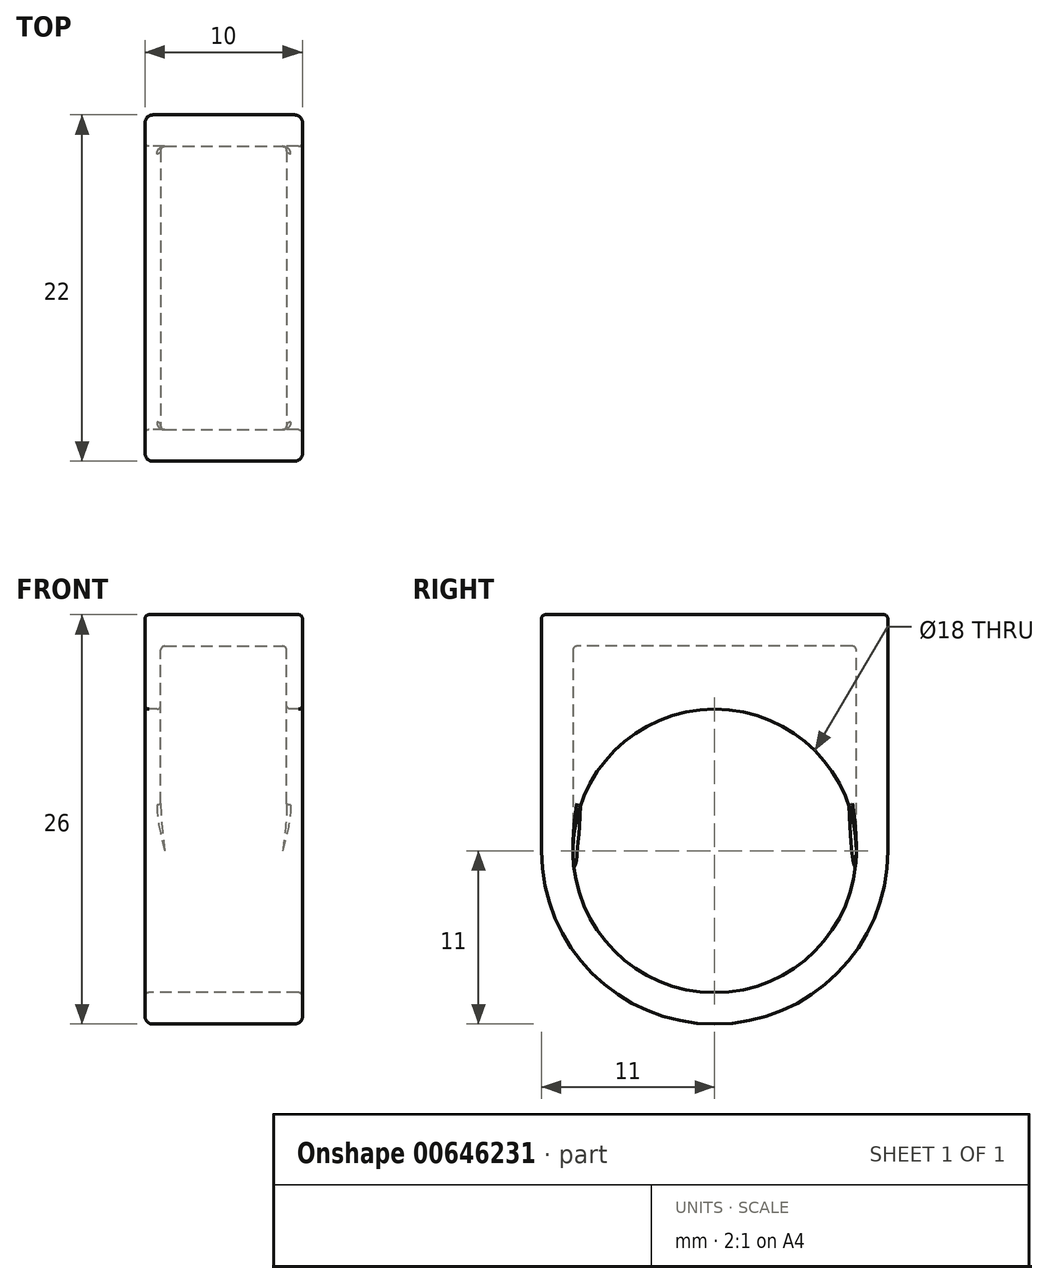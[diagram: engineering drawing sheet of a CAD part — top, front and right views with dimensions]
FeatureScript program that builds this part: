
annotation { "Feature Type Name" : "Feature", "Feature Type Description" : "" }
export const myFeature = defineFeature(function(context is Context, id is Id, definition is map)
    precondition{}
    {
        {
            var Q0;
            Q0=qCreatedBy(makeId("Right.planeOp"),FACE);
            var sketch = newSketch(context, id + "F0", { "sketchPlane" : qUnion([Q0])});
            skCircle(sketch, "E0", {"center": v(0, 0) * mm, "radius": 9 * mm});
            skArc(sketch, "E1", {"start": v(-11, 0) * mm, "mid": v(0, -11) * mm, "end": v(11, 0) * mm});
            skLineSegment(sketch, "E2", {"start": v(-11, 0) * mm, "end": v(-11, 15) * mm});
            skLineSegment(sketch, "E3", {"start": v(11, 0) * mm, "end": v(11, 15) * mm});
            skLineSegment(sketch, "E4", {"start": v(-11, 15) * mm, "end": v(11, 15) * mm});
            skSolve(sketch);
        }
        {
            var Q0;
            Q0 = qSketchRegion(id + "F0", true);
            extrude(context, id + "F1", {"entities" : qUnion([Q0]), "endBound" : BoundingType.SYMMETRIC, "depth" : 10 * mm, "offsetDistance" : 25 * mm});
        }
        {
            var Q0;
            Q0=qCreatedBy(makeId("Right.planeOp"),FACE);
            var sketch = newSketch(context, id + "F2", { "sketchPlane" : qUnion([Q0])});
            skLineSegment(sketch, "E5.0", {"start": v(9, 13) * mm, "end": v(-9, 13) * mm});
            skLineSegment(sketch, "E5.1", {"start": v(9, 0) * mm, "end": v(9, 13) * mm});
            skArc(sketch, "E5.2", {"start": v(-9, 0) * mm, "mid": v(0, -9) * mm, "end": v(9, 0) * mm});
            skLineSegment(sketch, "E5.3", {"start": v(-9, 13) * mm, "end": v(-9, 0) * mm});
            skSolve(sketch);
        }
        {
            var Q0;
            Q0 = qSketchRegion(id + "F2", true);
            extrude(context, id + "F3", {"entities" : qUnion([Q0]), "operationType" : NewBodyOperationType.REMOVE, "endBound" : BoundingType.SYMMETRIC, "oppositeDirection" : true, "depth" : 8 * mm, "offsetDistance" : 25 * mm});
        }
        {
            var Q0;
            Q0=makeQuery(id+"F1.opExtrude","CAP_EDGE",EDGE,{"disambiguationData":[OSD([sQuery(id+"F0.wireOp",EDGE,"E2")])],"isStart":false});
            var Q1;
            Q1=makeQuery(id+"F1.opExtrude","CAP_EDGE",EDGE,{"disambiguationData":[OSD([sQuery(id+"F0.wireOp",EDGE,"E2")])],"isStart":true});
            fillet(context, id + "F4", {"entities" : qUnion([Q0, Q1]), "radius" : .5 * mm, "tangentPropagation" : true, "allowEdgeOverflow" : false});
        }
        {
            var Q0;
            {var subQ0=sQuery(id+"F0.wireOp",EDGE,"E1");Q0=makeQuery(id+"F4.opFillet","BLEND_EDGE",EDGE,{"blendedFrom":[makeQuery(id+"F1.opExtrude","CAP_EDGE",EDGE,{"disambiguationData":[OSD([subQ0])],"isStart":true}),makeQuery(id+"F1.opExtrude","CAP_FACE",FACE,{"disambiguationData":[OSD([sQuery(id+"F0.wireOp",EDGE,"E0"),subQ0,sQuery(id+"F0.wireOp",EDGE,"E2"),sQuery(id+"F0.wireOp",EDGE,"E3"),sQuery(id+"F0.wireOp",EDGE,"E4")])],"isStart":true})],"blendedInto":[makeQuery(id+"F1.opExtrude","CAP_FACE",FACE,{"disambiguationData":[OSD([sQuery(id+"F0.wireOp",EDGE,"E0"),subQ0,sQuery(id+"F0.wireOp",EDGE,"E2"),sQuery(id+"F0.wireOp",EDGE,"E3"),sQuery(id+"F0.wireOp",EDGE,"E4")])],"isStart":true})]});}
            var Q1;
            Q1=makeQuery(id+"F1.opExtrude","CAP_EDGE",EDGE,{"disambiguationData":[OSD([sQuery(id+"F0.wireOp",EDGE,"E0")])],"isStart":true});
            var Q2;
            Q2=makeQuery(id+"F4.opFillet","BLEND_EDGE",EDGE,{"blendedFrom":[makeQuery(id+"F1.opExtrude","CAP_EDGE",EDGE,{"disambiguationData":[OSD([sQuery(id+"F0.wireOp",EDGE,"E2")])],"isStart":true}),makeQuery(id+"F1.opExtrude","SWEPT_FACE",FACE,{"disambiguationData":[OSD([sQuery(id+"F0.wireOp",EDGE,"E4")])]})],"blendedInto":[makeQuery(id+"F1.opExtrude","SWEPT_FACE",FACE,{"disambiguationData":[OSD([sQuery(id+"F0.wireOp",EDGE,"E4")])]})]});
            var Q3;
            Q3=makeQuery(id+"F3.boolean.opBoolean","COPY",EDGE,{"derivedFrom":makeQuery(id+"F3.opExtrude","SWEPT_EDGE",EDGE,{"disambiguationData":[OSD([sQuery(id+"F2.wireOp",EDGE,"E5.1"),sQuery(id+"F2.wireOp",EDGE,"E5.2")])]})});
            var Q4;
            Q4=makeQuery(id+"F3.boolean.opBoolean","INTERSECT",EDGE,{"derivedFrom":[makeQuery(id+"F1.opExtrude","SWEPT_FACE",FACE,{"disambiguationData":[OSD([sQuery(id+"F0.wireOp",EDGE,"E0")])]}),makeQuery(id+"F3.opExtrude","CAP_FACE",FACE,{"disambiguationData":[OSD([sQuery(id+"F2.wireOp",EDGE,"E5.0"),sQuery(id+"F2.wireOp",EDGE,"E5.1"),sQuery(id+"F2.wireOp",EDGE,"E5.2"),sQuery(id+"F2.wireOp",EDGE,"E5.3")])],"isStart":false})]});
            var Q5;
            {var subQ0=sQuery(id+"F0.wireOp",EDGE,"E1");Q5=makeQuery(id+"F4.opFillet","BLEND_EDGE",EDGE,{"blendedFrom":[makeQuery(id+"F1.opExtrude","CAP_EDGE",EDGE,{"disambiguationData":[OSD([subQ0])],"isStart":true}),makeQuery(id+"F1.opExtrude","SWEPT_FACE",FACE,{"disambiguationData":[OSD([subQ0])]})],"blendedInto":[makeQuery(id+"F1.opExtrude","SWEPT_FACE",FACE,{"disambiguationData":[OSD([subQ0])]})]});}
            var Q6;
            {var subQ0=sQuery(id+"F0.wireOp",EDGE,"E1");Q6=makeQuery(id+"F4.opFillet","BLEND_EDGE",EDGE,{"blendedFrom":[makeQuery(id+"F1.opExtrude","CAP_EDGE",EDGE,{"disambiguationData":[OSD([subQ0])],"isStart":false}),makeQuery(id+"F1.opExtrude","SWEPT_FACE",FACE,{"disambiguationData":[OSD([subQ0])]})],"blendedInto":[makeQuery(id+"F1.opExtrude","SWEPT_FACE",FACE,{"disambiguationData":[OSD([subQ0])]})]});}
            var Q7;
            Q7=makeQuery(id+"F1.opExtrude","CAP_EDGE",EDGE,{"disambiguationData":[OSD([sQuery(id+"F0.wireOp",EDGE,"E4")])],"isStart":true});
            var Q8;
            Q8=makeQuery(id+"F1.opExtrude","CAP_EDGE",EDGE,{"disambiguationData":[OSD([sQuery(id+"F0.wireOp",EDGE,"E4")])],"isStart":false});
            var Q9;
            Q9=makeQuery(id+"F4.opFillet","BLEND_EDGE",EDGE,{"blendedFrom":[makeQuery(id+"F1.opExtrude","CAP_EDGE",EDGE,{"disambiguationData":[OSD([sQuery(id+"F0.wireOp",EDGE,"E1")])],"isStart":true}),makeQuery(id+"F1.opExtrude","CAP_EDGE",EDGE,{"disambiguationData":[OSD([sQuery(id+"F0.wireOp",EDGE,"E2")])],"isStart":true})],"blendedInto":[]});
            var Q10;
            Q10=makeQuery(id+"F1.opExtrude","SWEPT_EDGE",EDGE,{"disambiguationData":[OSD([sQuery(id+"F0.wireOp",EDGE,"E3"),sQuery(id+"F0.wireOp",EDGE,"E4")])]});
            var Q11;
            Q11=makeQuery(id+"F4.opFillet","BLEND_EDGE",EDGE,{"blendedFrom":[makeQuery(id+"F1.opExtrude","CAP_EDGE",EDGE,{"disambiguationData":[OSD([sQuery(id+"F0.wireOp",EDGE,"E1")])],"isStart":true}),makeQuery(id+"F1.opExtrude","CAP_EDGE",EDGE,{"disambiguationData":[OSD([sQuery(id+"F0.wireOp",EDGE,"E3")])],"isStart":true})],"blendedInto":[]});
            var Q12;
            Q12=makeQuery(id+"F1.opExtrude","SWEPT_EDGE",EDGE,{"disambiguationData":[OSD([sQuery(id+"F0.wireOp",EDGE,"E2"),sQuery(id+"F0.wireOp",EDGE,"E4")])]});
            var Q13;
            Q13=makeQuery(id+"F1.opExtrude","CAP_EDGE",EDGE,{"disambiguationData":[OSD([sQuery(id+"F0.wireOp",EDGE,"E0")])],"isStart":false});
            var Q14;
            Q14=makeQuery(id+"F1.opExtrude","SWEPT_EDGE",EDGE,{"disambiguationData":[OSD([sQuery(id+"F0.wireOp",EDGE,"E1"),sQuery(id+"F0.wireOp",EDGE,"E3")])]});
            var Q15;
            Q15=makeQuery(id+"F1.opExtrude","SWEPT_EDGE",EDGE,{"disambiguationData":[OSD([sQuery(id+"F0.wireOp",EDGE,"E1"),sQuery(id+"F0.wireOp",EDGE,"E2")])]});
            var Q16;
            {var subQ0=sQuery(id+"F0.wireOp",EDGE,"E2");Q16=makeQuery(id+"F4.opFillet","BLEND_EDGE",EDGE,{"blendedFrom":[makeQuery(id+"F1.opExtrude","CAP_EDGE",EDGE,{"disambiguationData":[OSD([subQ0])],"isStart":false}),makeQuery(id+"F1.opExtrude","CAP_FACE",FACE,{"disambiguationData":[OSD([sQuery(id+"F0.wireOp",EDGE,"E0"),sQuery(id+"F0.wireOp",EDGE,"E1"),subQ0,sQuery(id+"F0.wireOp",EDGE,"E3"),sQuery(id+"F0.wireOp",EDGE,"E4")])],"isStart":false})],"blendedInto":[makeQuery(id+"F1.opExtrude","CAP_FACE",FACE,{"disambiguationData":[OSD([sQuery(id+"F0.wireOp",EDGE,"E0"),sQuery(id+"F0.wireOp",EDGE,"E1"),subQ0,sQuery(id+"F0.wireOp",EDGE,"E3"),sQuery(id+"F0.wireOp",EDGE,"E4")])],"isStart":false})]});}
            var Q17;
            {var subQ0=sQuery(id+"F0.wireOp",EDGE,"E2");Q17=makeQuery(id+"F4.opFillet","BLEND_EDGE",EDGE,{"blendedFrom":[makeQuery(id+"F1.opExtrude","CAP_EDGE",EDGE,{"disambiguationData":[OSD([subQ0])],"isStart":true}),makeQuery(id+"F1.opExtrude","SWEPT_FACE",FACE,{"disambiguationData":[OSD([subQ0])]})],"blendedInto":[makeQuery(id+"F1.opExtrude","SWEPT_FACE",FACE,{"disambiguationData":[OSD([subQ0])]})]});}
            var Q18;
            Q18=makeQuery(id+"F3.boolean.opBoolean","COPY",EDGE,{"derivedFrom":makeQuery(id+"F3.opExtrude","SWEPT_EDGE",EDGE,{"disambiguationData":[OSD([sQuery(id+"F2.wireOp",EDGE,"E5.0"),sQuery(id+"F2.wireOp",EDGE,"E5.1")])]})});
            var Q19;
            Q19=makeQuery(id+"F3.boolean.opBoolean","COPY",EDGE,{"derivedFrom":makeQuery(id+"F3.opExtrude","SWEPT_EDGE",EDGE,{"disambiguationData":[OSD([sQuery(id+"F2.wireOp",EDGE,"E5.0"),sQuery(id+"F2.wireOp",EDGE,"E5.3")])]})});
            var Q20;
            Q20=makeQuery(id+"F3.boolean.opBoolean","COPY",EDGE,{"derivedFrom":makeQuery(id+"F3.opExtrude","SWEPT_EDGE",EDGE,{"disambiguationData":[OSD([sQuery(id+"F2.wireOp",EDGE,"E5.2"),sQuery(id+"F2.wireOp",EDGE,"E5.3")])]})});
            var Q21;
            Q21=makeQuery(id+"F3.boolean.opBoolean","COPY",EDGE,{"derivedFrom":makeQuery(id+"F3.opExtrude","CAP_EDGE",EDGE,{"disambiguationData":[OSD([sQuery(id+"F2.wireOp",EDGE,"E5.0")])],"isStart":true})});
            var Q22;
            Q22=makeQuery(id+"F3.boolean.opBoolean","COPY",EDGE,{"derivedFrom":makeQuery(id+"F3.opExtrude","CAP_EDGE",EDGE,{"disambiguationData":[OSD([sQuery(id+"F2.wireOp",EDGE,"E5.0")])],"isStart":false})});
            var Q23;
            Q23=makeQuery(id+"F3.boolean.opBoolean","COPY",EDGE,{"derivedFrom":makeQuery(id+"F3.opExtrude","CAP_EDGE",EDGE,{"disambiguationData":[OSD([sQuery(id+"F2.wireOp",EDGE,"E5.1")])],"isStart":false})});
            var Q24;
            {var subQ0=sQuery(id+"F0.wireOp",EDGE,"E1");Q24=makeQuery(id+"F4.opFillet","BLEND_EDGE",EDGE,{"blendedFrom":[makeQuery(id+"F1.opExtrude","CAP_EDGE",EDGE,{"disambiguationData":[OSD([subQ0])],"isStart":false}),makeQuery(id+"F1.opExtrude","CAP_FACE",FACE,{"disambiguationData":[OSD([sQuery(id+"F0.wireOp",EDGE,"E0"),subQ0,sQuery(id+"F0.wireOp",EDGE,"E2"),sQuery(id+"F0.wireOp",EDGE,"E3"),sQuery(id+"F0.wireOp",EDGE,"E4")])],"isStart":false})],"blendedInto":[makeQuery(id+"F1.opExtrude","CAP_FACE",FACE,{"disambiguationData":[OSD([sQuery(id+"F0.wireOp",EDGE,"E0"),subQ0,sQuery(id+"F0.wireOp",EDGE,"E2"),sQuery(id+"F0.wireOp",EDGE,"E3"),sQuery(id+"F0.wireOp",EDGE,"E4")])],"isStart":false})]});}
            var Q25;
            {var subQ0=sQuery(id+"F0.wireOp",EDGE,"E2");Q25=makeQuery(id+"F4.opFillet","BLEND_EDGE",EDGE,{"blendedFrom":[makeQuery(id+"F1.opExtrude","CAP_EDGE",EDGE,{"disambiguationData":[OSD([subQ0])],"isStart":true}),makeQuery(id+"F1.opExtrude","CAP_FACE",FACE,{"disambiguationData":[OSD([sQuery(id+"F0.wireOp",EDGE,"E0"),sQuery(id+"F0.wireOp",EDGE,"E1"),subQ0,sQuery(id+"F0.wireOp",EDGE,"E3"),sQuery(id+"F0.wireOp",EDGE,"E4")])],"isStart":true})],"blendedInto":[makeQuery(id+"F1.opExtrude","CAP_FACE",FACE,{"disambiguationData":[OSD([sQuery(id+"F0.wireOp",EDGE,"E0"),sQuery(id+"F0.wireOp",EDGE,"E1"),subQ0,sQuery(id+"F0.wireOp",EDGE,"E3"),sQuery(id+"F0.wireOp",EDGE,"E4")])],"isStart":true})]});}
            var Q26;
            {var subQ0=sQuery(id+"F0.wireOp",EDGE,"E2");Q26=makeQuery(id+"F4.opFillet","BLEND_EDGE",EDGE,{"blendedFrom":[makeQuery(id+"F1.opExtrude","CAP_EDGE",EDGE,{"disambiguationData":[OSD([subQ0])],"isStart":false}),makeQuery(id+"F1.opExtrude","SWEPT_FACE",FACE,{"disambiguationData":[OSD([subQ0])]})],"blendedInto":[makeQuery(id+"F1.opExtrude","SWEPT_FACE",FACE,{"disambiguationData":[OSD([subQ0])]})]});}
            var Q27;
            Q27=makeQuery(id+"F4.opFillet","BLEND_EDGE",EDGE,{"blendedFrom":[makeQuery(id+"F1.opExtrude","CAP_EDGE",EDGE,{"disambiguationData":[OSD([sQuery(id+"F0.wireOp",EDGE,"E2")])],"isStart":false}),makeQuery(id+"F1.opExtrude","SWEPT_FACE",FACE,{"disambiguationData":[OSD([sQuery(id+"F0.wireOp",EDGE,"E4")])]})],"blendedInto":[makeQuery(id+"F1.opExtrude","SWEPT_FACE",FACE,{"disambiguationData":[OSD([sQuery(id+"F0.wireOp",EDGE,"E4")])]})]});
            var Q28;
            {var subQ0=sQuery(id+"F0.wireOp",EDGE,"E3");Q28=makeQuery(id+"F4.opFillet","BLEND_EDGE",EDGE,{"blendedFrom":[makeQuery(id+"F1.opExtrude","CAP_EDGE",EDGE,{"disambiguationData":[OSD([subQ0])],"isStart":true}),makeQuery(id+"F1.opExtrude","CAP_FACE",FACE,{"disambiguationData":[OSD([sQuery(id+"F0.wireOp",EDGE,"E0"),sQuery(id+"F0.wireOp",EDGE,"E1"),sQuery(id+"F0.wireOp",EDGE,"E2"),subQ0,sQuery(id+"F0.wireOp",EDGE,"E4")])],"isStart":true})],"blendedInto":[makeQuery(id+"F1.opExtrude","CAP_FACE",FACE,{"disambiguationData":[OSD([sQuery(id+"F0.wireOp",EDGE,"E0"),sQuery(id+"F0.wireOp",EDGE,"E1"),sQuery(id+"F0.wireOp",EDGE,"E2"),subQ0,sQuery(id+"F0.wireOp",EDGE,"E4")])],"isStart":true})]});}
            var Q29;
            {var subQ0=sQuery(id+"F0.wireOp",EDGE,"E3");Q29=makeQuery(id+"F4.opFillet","BLEND_EDGE",EDGE,{"blendedFrom":[makeQuery(id+"F1.opExtrude","CAP_EDGE",EDGE,{"disambiguationData":[OSD([subQ0])],"isStart":true}),makeQuery(id+"F1.opExtrude","SWEPT_FACE",FACE,{"disambiguationData":[OSD([subQ0])]})],"blendedInto":[makeQuery(id+"F1.opExtrude","SWEPT_FACE",FACE,{"disambiguationData":[OSD([subQ0])]})]});}
            var Q30;
            Q30=makeQuery(id+"F4.opFillet","BLEND_EDGE",EDGE,{"blendedFrom":[makeQuery(id+"F1.opExtrude","CAP_EDGE",EDGE,{"disambiguationData":[OSD([sQuery(id+"F0.wireOp",EDGE,"E3")])],"isStart":true}),makeQuery(id+"F1.opExtrude","SWEPT_FACE",FACE,{"disambiguationData":[OSD([sQuery(id+"F0.wireOp",EDGE,"E4")])]})],"blendedInto":[makeQuery(id+"F1.opExtrude","SWEPT_FACE",FACE,{"disambiguationData":[OSD([sQuery(id+"F0.wireOp",EDGE,"E4")])]})]});
            var Q31;
            {var subQ0=sQuery(id+"F0.wireOp",EDGE,"E3");Q31=makeQuery(id+"F4.opFillet","BLEND_EDGE",EDGE,{"blendedFrom":[makeQuery(id+"F1.opExtrude","CAP_EDGE",EDGE,{"disambiguationData":[OSD([subQ0])],"isStart":false}),makeQuery(id+"F1.opExtrude","CAP_FACE",FACE,{"disambiguationData":[OSD([sQuery(id+"F0.wireOp",EDGE,"E0"),sQuery(id+"F0.wireOp",EDGE,"E1"),sQuery(id+"F0.wireOp",EDGE,"E2"),subQ0,sQuery(id+"F0.wireOp",EDGE,"E4")])],"isStart":false})],"blendedInto":[makeQuery(id+"F1.opExtrude","CAP_FACE",FACE,{"disambiguationData":[OSD([sQuery(id+"F0.wireOp",EDGE,"E0"),sQuery(id+"F0.wireOp",EDGE,"E1"),sQuery(id+"F0.wireOp",EDGE,"E2"),subQ0,sQuery(id+"F0.wireOp",EDGE,"E4")])],"isStart":false})]});}
            var Q32;
            Q32=makeQuery(id+"F4.opFillet","BLEND_EDGE",EDGE,{"blendedFrom":[makeQuery(id+"F1.opExtrude","CAP_EDGE",EDGE,{"disambiguationData":[OSD([sQuery(id+"F0.wireOp",EDGE,"E3")])],"isStart":false}),makeQuery(id+"F1.opExtrude","SWEPT_FACE",FACE,{"disambiguationData":[OSD([sQuery(id+"F0.wireOp",EDGE,"E4")])]})],"blendedInto":[makeQuery(id+"F1.opExtrude","SWEPT_FACE",FACE,{"disambiguationData":[OSD([sQuery(id+"F0.wireOp",EDGE,"E4")])]})]});
            var Q33;
            Q33=makeQuery(id+"F3.boolean.opBoolean","COPY",EDGE,{"derivedFrom":makeQuery(id+"F3.opExtrude","CAP_EDGE",EDGE,{"disambiguationData":[OSD([sQuery(id+"F2.wireOp",EDGE,"E5.1")])],"isStart":true})});
            var Q34;
            Q34=makeQuery(id+"F3.boolean.opBoolean","COPY",EDGE,{"derivedFrom":makeQuery(id+"F3.opExtrude","CAP_EDGE",EDGE,{"disambiguationData":[OSD([sQuery(id+"F2.wireOp",EDGE,"E5.3")])],"isStart":true})});
            var Q35;
            Q35=makeQuery(id+"F3.boolean.opBoolean","COPY",EDGE,{"derivedFrom":makeQuery(id+"F3.opExtrude","CAP_EDGE",EDGE,{"disambiguationData":[OSD([sQuery(id+"F2.wireOp",EDGE,"E5.3")])],"isStart":false})});
            var Q36;
            Q36=makeQuery(id+"F3.boolean.opBoolean","INTERSECT",EDGE,{"derivedFrom":[makeQuery(id+"F1.opExtrude","SWEPT_FACE",FACE,{"disambiguationData":[OSD([sQuery(id+"F0.wireOp",EDGE,"E0")])]}),makeQuery(id+"F3.opExtrude","CAP_FACE",FACE,{"disambiguationData":[OSD([sQuery(id+"F2.wireOp",EDGE,"E5.0"),sQuery(id+"F2.wireOp",EDGE,"E5.1"),sQuery(id+"F2.wireOp",EDGE,"E5.2"),sQuery(id+"F2.wireOp",EDGE,"E5.3")])],"isStart":true})]});
            var Q37;
            Q37=makeQuery(id+"F4.opFillet","BLEND_EDGE",EDGE,{"blendedFrom":[makeQuery(id+"F1.opExtrude","CAP_EDGE",EDGE,{"disambiguationData":[OSD([sQuery(id+"F0.wireOp",EDGE,"E1")])],"isStart":false}),makeQuery(id+"F1.opExtrude","CAP_EDGE",EDGE,{"disambiguationData":[OSD([sQuery(id+"F0.wireOp",EDGE,"E2")])],"isStart":false})],"blendedInto":[]});
            var Q38;
            {var subQ0=sQuery(id+"F0.wireOp",EDGE,"E3");Q38=makeQuery(id+"F4.opFillet","BLEND_EDGE",EDGE,{"blendedFrom":[makeQuery(id+"F1.opExtrude","CAP_EDGE",EDGE,{"disambiguationData":[OSD([subQ0])],"isStart":false}),makeQuery(id+"F1.opExtrude","SWEPT_FACE",FACE,{"disambiguationData":[OSD([subQ0])]})],"blendedInto":[makeQuery(id+"F1.opExtrude","SWEPT_FACE",FACE,{"disambiguationData":[OSD([subQ0])]})]});}
            var Q39;
            Q39=makeQuery(id+"F4.opFillet","BLEND_EDGE",EDGE,{"blendedFrom":[makeQuery(id+"F1.opExtrude","CAP_EDGE",EDGE,{"disambiguationData":[OSD([sQuery(id+"F0.wireOp",EDGE,"E1")])],"isStart":false}),makeQuery(id+"F1.opExtrude","CAP_EDGE",EDGE,{"disambiguationData":[OSD([sQuery(id+"F0.wireOp",EDGE,"E3")])],"isStart":false})],"blendedInto":[]});
            fillet(context, id + "F5", {"entities" : qUnion([Q0, Q1, Q2, Q3, Q4, Q5, Q6, Q7, Q8, Q9, Q10, Q11, Q12, Q13, Q14, Q15, Q16, Q17, Q18, Q19, Q20, Q21, Q22, Q23, Q24, Q25, Q26, Q27, Q28, Q29, Q30, Q31, Q32, Q33, Q34, Q35, Q36, Q37, Q38, Q39]), "radius" : .25 * mm, "tangentPropagation" : true, "allowEdgeOverflow" : false});
        }
    });
